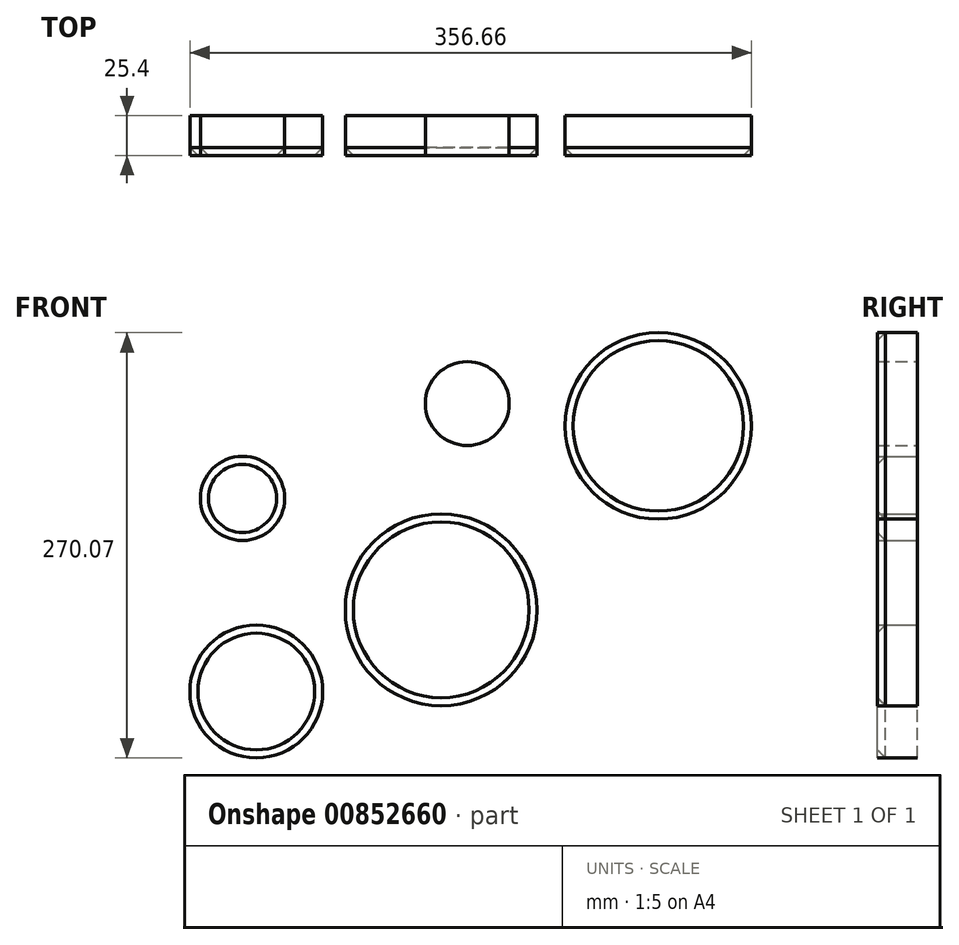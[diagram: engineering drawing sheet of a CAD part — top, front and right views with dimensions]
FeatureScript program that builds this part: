
annotation { "Feature Type Name" : "Feature", "Feature Type Description" : "" }
export const myFeature = defineFeature(function(context is Context, id is Id, definition is map)
    precondition{}
    {
        {
            var Q0;
            Q0=qCreatedBy(makeId("Front.planeOp"),FACE);
            var sketch = newSketch(context, id + "F0", { "sketchPlane" : qUnion([Q0])});
            skCircle(sketch, "E0", {"center": v(-115.02, 25.77) * mm, "radius": 26.75 * mm});
            skCircle(sketch, "E1", {"center": v(-106.25, -96.91) * mm, "radius": 42.16 * mm});
            skCircle(sketch, "E2", {"center": v(11.17, -44.99) * mm, "radius": 60.92 * mm});
            skCircle(sketch, "E3", {"center": v(149.05, 71.8) * mm, "radius": 59.2 * mm});
            skCircle(sketch, "E4", {"center": v(27.74, 85.98) * mm, "radius": 26.63 * mm});
            skSolve(sketch);
        }
        {
            var Q0;
            Q0 = qSketchRegion(id + "F0", true);
            extrude(context, id + "F1", {"entities" : qUnion([Q0]), "depth" : 25.4 * mm, "offsetDistance" : 25.4 * mm});
        }
        {
            var Q0;
            Q0 = qSketchRegion(id + "F0", true);
            extrude(context, id + "F2", {"entities" : qUnion([Q0]), "depth" : 25.4 * mm, "offsetDistance" : 25.4 * mm});
        }
        {
            var Q0;
            Q0=makeQuery(id+"F1.opExtrude","CAP_FACE",FACE,{"disambiguationData":[OSD([sQuery(id+"F0.wireOp",EDGE,"E0")])],"isStart":false});
            var Q1;
            Q1=makeQuery(id+"F1.opExtrude","CAP_FACE",FACE,{"disambiguationData":[OSD([sQuery(id+"F0.wireOp",EDGE,"E1")])],"isStart":false});
            var Q2;
            Q2=makeQuery(id+"F1.opExtrude","CAP_FACE",FACE,{"disambiguationData":[OSD([sQuery(id+"F0.wireOp",EDGE,"E2")])],"isStart":false});
            var Q3;
            Q3=makeQuery(id+"F1.opExtrude","CAP_FACE",FACE,{"disambiguationData":[OSD([sQuery(id+"F0.wireOp",EDGE,"E3")])],"isStart":false});
            chamfer(context, id + "F3", {"entities" : qUnion([Q0, Q1, Q2, Q3]), "width" : 5.08 * mm, "tangentPropagation" : true});
        }
    });
